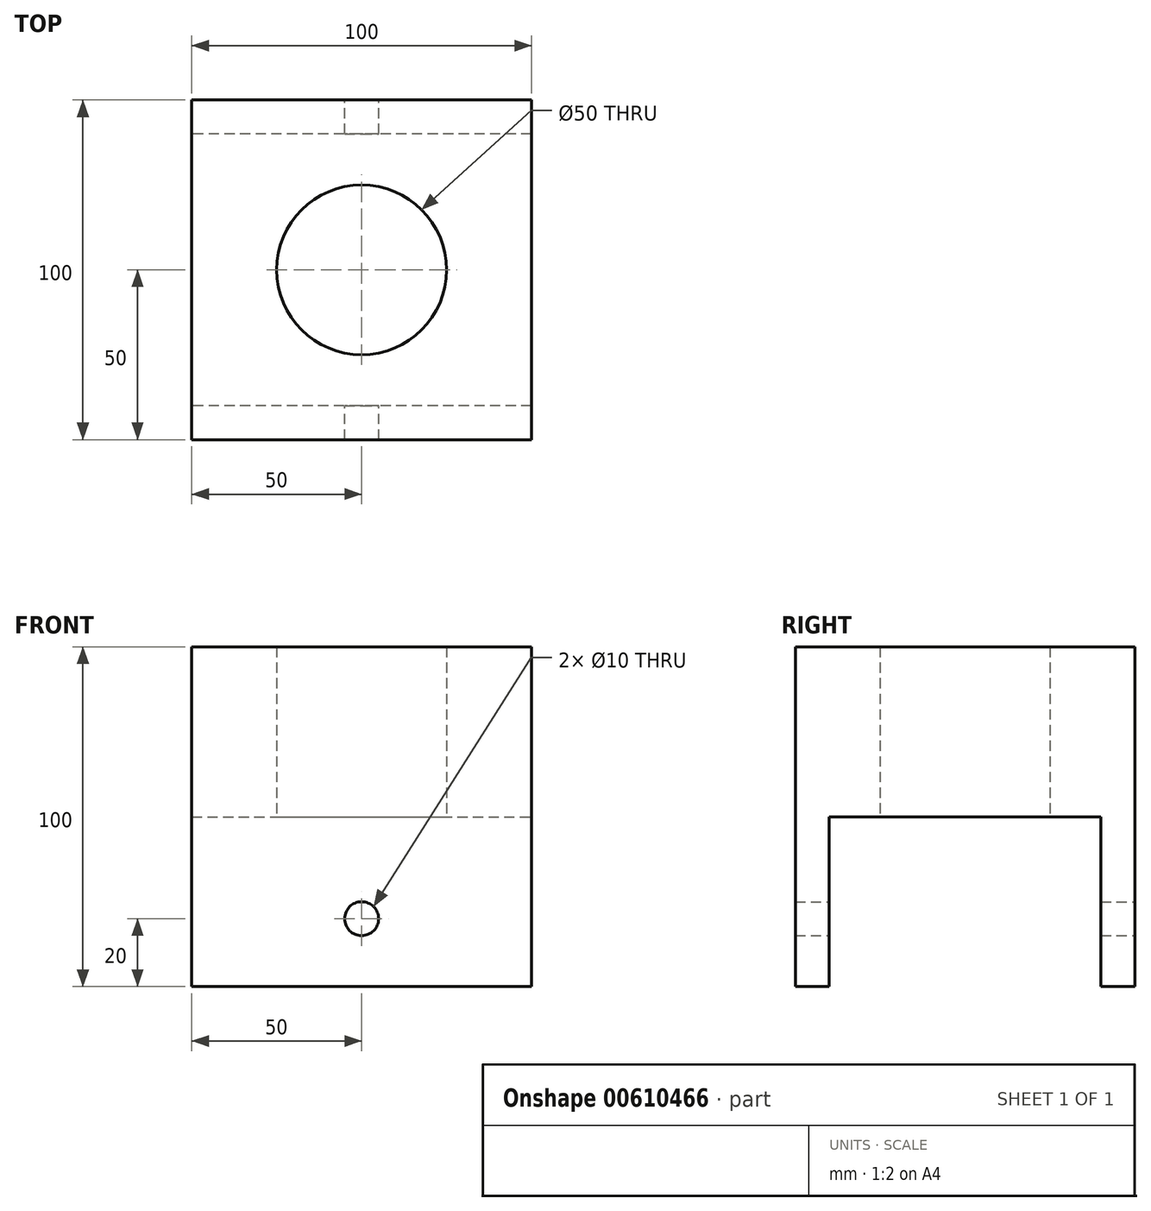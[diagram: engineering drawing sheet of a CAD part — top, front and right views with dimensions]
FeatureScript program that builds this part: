
annotation { "Feature Type Name" : "Feature", "Feature Type Description" : "" }
export const myFeature = defineFeature(function(context is Context, id is Id, definition is map)
    precondition{}
    {
        {
            var Q0;
            Q0=qCreatedBy(makeId("Top.planeOp"),FACE);
            var sketch = newSketch(context, id + "F0", { "sketchPlane" : qUnion([Q0])});
            skLineSegment(sketch, "E0.bottom", {"start": v(50, -50) * mm, "end": v(-50, -50) * mm});
            skLineSegment(sketch, "E0.top", {"start": v(50, 50) * mm, "end": v(-50, 50) * mm});
            skLineSegment(sketch, "E0.left", {"start": v(50, -50) * mm, "end": v(50, 50) * mm});
            skLineSegment(sketch, "E0.right", {"start": v(-50, -50) * mm, "end": v(-50, 50) * mm});
            skPoint(sketch, "E0.middle", {"position": v(0, 0) * mm});
            skCircle(sketch, "E1", {"center": v(0, 0) * mm, "radius": 25 * mm});
            skSolve(sketch);
        }
        {
            var Q0;
            Q0 = qSketchRegion(id + "F0", true);
            extrude(context, id + "F1", {"entities" : qUnion([Q0]), "depth" : 100 * mm, "offsetDistance" : 25 * mm});
        }
        {
            var Q0;
            Q0=makeQuery(id+"F1.opExtrude","SWEPT_FACE",FACE,{"disambiguationData":[OSD([sQuery(id+"F0.wireOp",EDGE,"E0.left")])]});
            var sketch = newSketch(context, id + "F2", { "sketchPlane" : qUnion([Q0])});
            skLineSegment(sketch, "E2.bottom", {"start": v(-40, -50) * mm, "end": v(40, -50) * mm});
            skLineSegment(sketch, "E2.top", {"start": v(-40, 50) * mm, "end": v(40, 50) * mm});
            skLineSegment(sketch, "E2.left", {"start": v(-40, -50) * mm, "end": v(-40, 50) * mm});
            skLineSegment(sketch, "E2.right", {"start": v(40, -50) * mm, "end": v(40, 50) * mm});
            skPoint(sketch, "E2.middle", {"position": v(0, 0) * mm});
            skSolve(sketch);
        }
        {
            var Q0;
            Q0 = qSketchRegion(id + "F2", true);
            extrude(context, id + "F3", {"entities" : qUnion([Q0]), "operationType" : NewBodyOperationType.REMOVE, "oppositeDirection" : true, "depth" : 100 * mm, "offsetDistance" : 25 * mm});
        }
        {
            var Q0;
            Q0=makeQuery(id+"F1.opExtrude","SWEPT_FACE",FACE,{"disambiguationData":[OSD([sQuery(id+"F0.wireOp",EDGE,"E0.top")])]});
            var sketch = newSketch(context, id + "F4", { "sketchPlane" : qUnion([Q0])});
            skCircle(sketch, "E3", {"center": v(0, 20) * mm, "radius": 5 * mm});
            skSolve(sketch);
        }
        {
            var Q0;
            Q0 = qSketchRegion(id + "F4", true);
            extrude(context, id + "F5", {"entities" : qUnion([Q0]), "operationType" : NewBodyOperationType.REMOVE, "oppositeDirection" : true, "depth" : 100 * mm, "offsetDistance" : 25 * mm});
        }
    });
